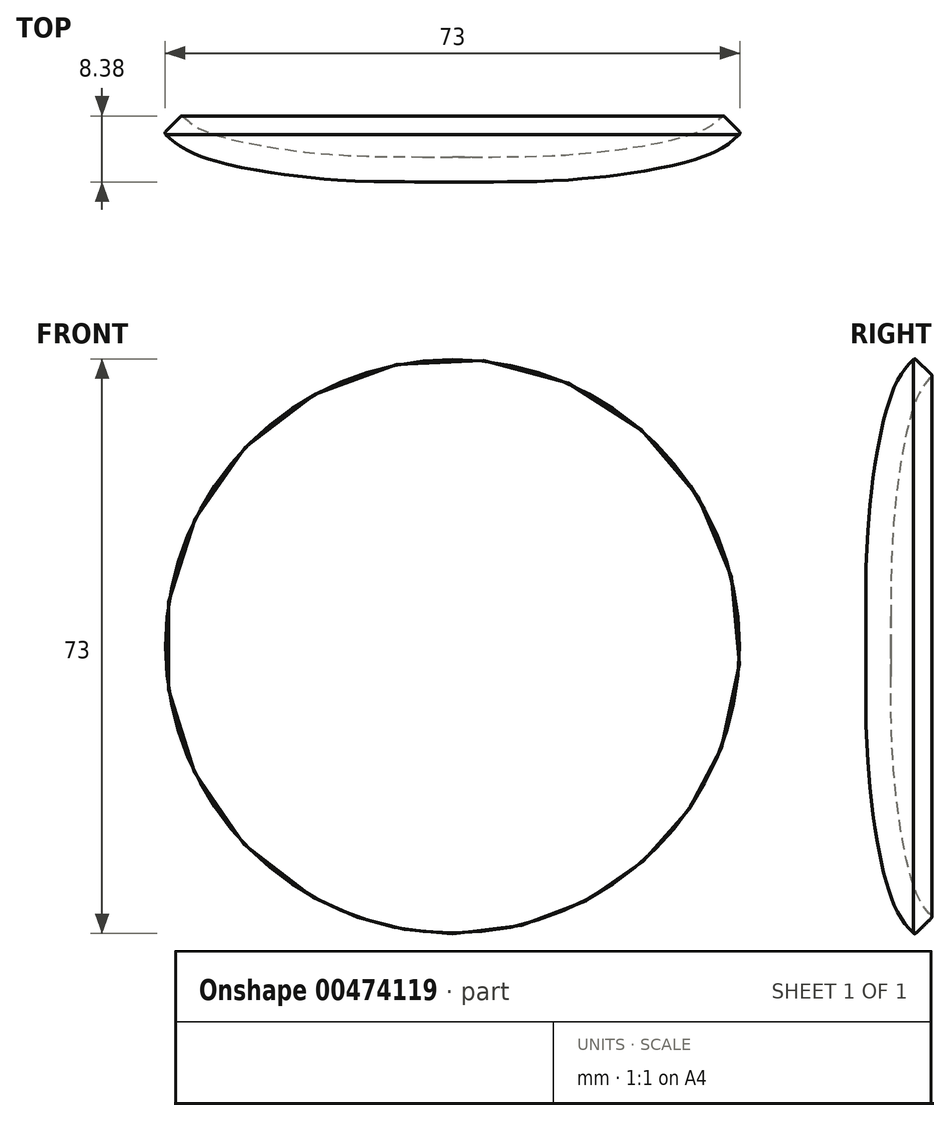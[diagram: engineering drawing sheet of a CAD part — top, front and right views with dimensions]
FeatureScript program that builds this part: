
annotation { "Feature Type Name" : "Feature", "Feature Type Description" : "" }
export const myFeature = defineFeature(function(context is Context, id is Id, definition is map)
    precondition{}
    {
        {
            var Q0;
            Q0=qCreatedBy(makeId("Top.planeOp"),FACE);
            var sketch = newSketch(context, id + "F0", { "sketchPlane" : qUnion([Q0])});
            skLineSegment(sketch, "E0", {"start": v(0, 0) * mm, "end": v(0, 3.18) * mm});
            skFitSpline(sketch, "E1", {"points": [v(0, 3.18) * mm, v(6.75, 3.18) * mm, v(18.5, 3.77) * mm, v(31.64, 6.53) * mm, v(34.4, 8.47) * mm], "startDerivative": vector(28.33, -0.13) * mm, "endDerivative": vector(12.9, 12.56) * mm});
            skFitSpline(sketch, "E2.0", {"points": [v(-0.01, 0) * mm, v(1.17, 0) * mm, v(2.94, -0.01) * mm, v(5.51, 0) * mm, v(8.27, 0) * mm, v(11.42, 0.07) * mm, v(14.93, 0.26) * mm, v(17.27, 0.45) * mm, v(19.23, 0.66) * mm, v(21.24, 0.9) * mm, v(23.8, 1.27) * mm, v(26.77, 1.81) * mm, v(29.08, 2.35) * mm, v(30.77, 2.82) * mm, v(31.75, 3.15) * mm, v(32.5, 3.44) * mm, v(33.03, 3.67) * mm, v(33.54, 3.91) * mm, v(34.17, 4.25) * mm, v(34.88, 4.7) * mm, v(35.6, 5.25) * mm, v(36.17, 5.77) * mm, v(36.47, 6.07) * mm, v(36.6, 6.2) * mm]});
            skLineSegment(sketch, "E3", {"start": v(34.4, 8.47) * mm, "end": v(36.6, 6.2) * mm});
            skSolve(sketch);
        }
        {
            var Q0;
            Q0=makeQuery(id+"F0.imprint","IMPRINT",FACE,{"disambiguationData":[TD([[makeQuery(id+"F0.imprint","IMPRINT",EDGE,{"derivedFrom":sQuery(id+"F0.wireOp",EDGE,"E0")}),-1.0]])]});
            var Q1;
            Q1=sQuery(id+"F0.wireOp",EDGE,"E0");
            revolve(context, id + "F1", {"entities" : qUnion([Q0]), "axis" : qUnion([Q1]), "revolveType" : RevolveType.FULL});
        }
        {
            var Q0;
            Q0=makeQuery(id+"F1.opRevolve","SWEPT_EDGE",EDGE,{"disambiguationData":[OSD([sQuery(id+"F0.wireOp",EDGE,"E2.0"),sQuery(id+"F0.wireOp",EDGE,"E3")])]});
            fillet(context, id + "F2", {"entities" : qUnion([Q0]), "radius" : 0.25 * mm, "tangentPropagation" : true, "allowEdgeOverflow" : false});
        }
        {
            var Q0;
            Q0=makeQuery(id+"F1.opRevolve","SWEPT_EDGE",EDGE,{"disambiguationData":[OSD([sQuery(id+"F0.wireOp",EDGE,"E1"),sQuery(id+"F0.wireOp",EDGE,"E3")])]});
            fillet(context, id + "F3", {"entities" : qUnion([Q0]), "radius" : 0.25 * mm, "tangentPropagation" : true, "allowEdgeOverflow" : false});
        }
    });
